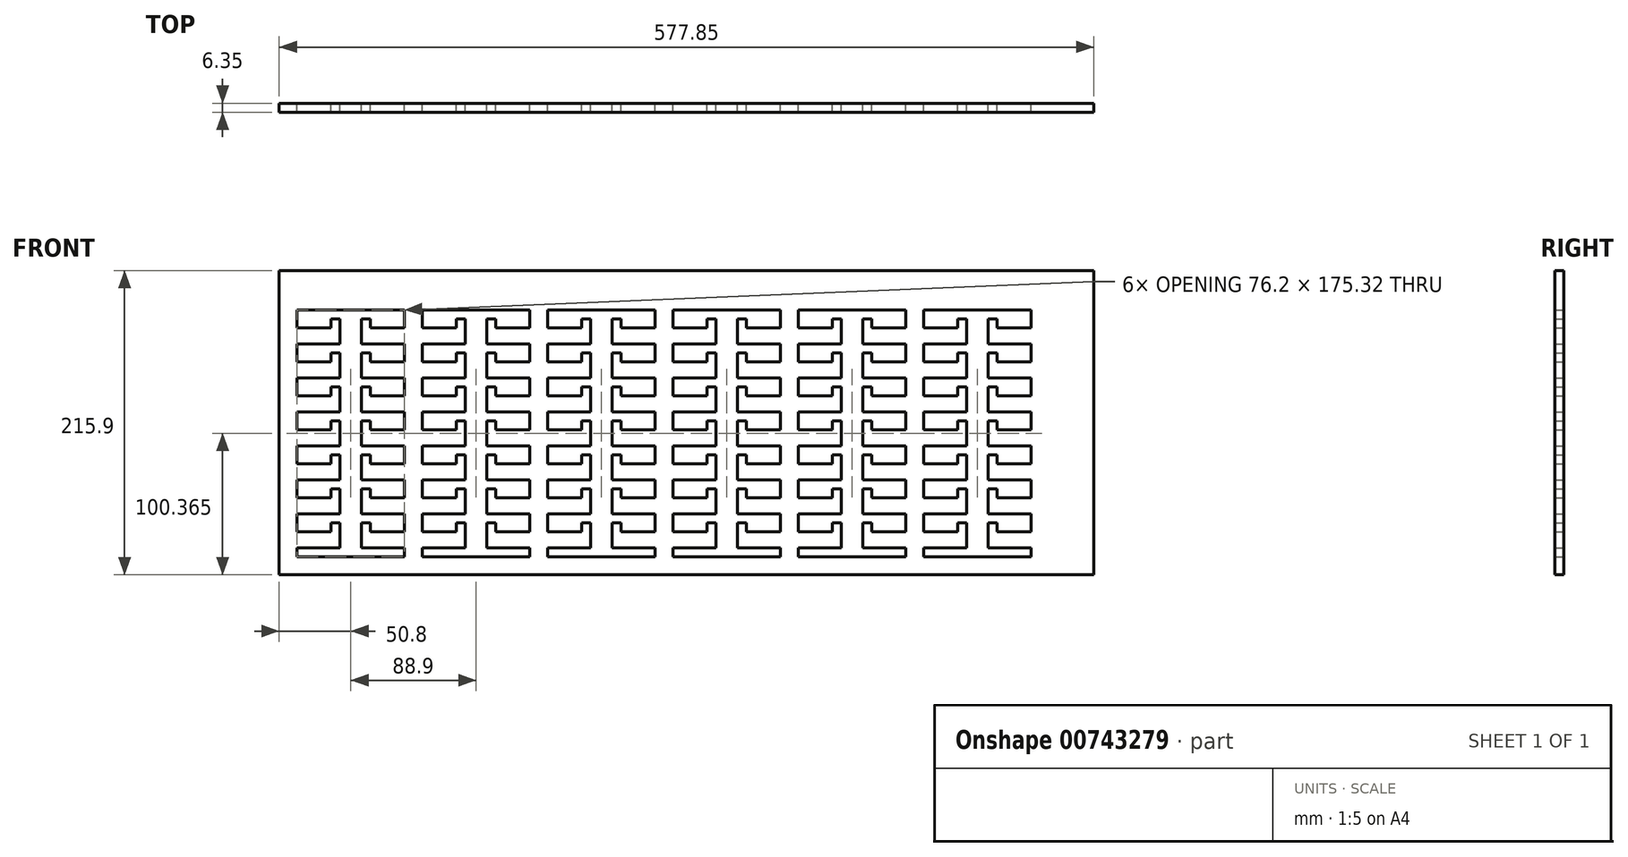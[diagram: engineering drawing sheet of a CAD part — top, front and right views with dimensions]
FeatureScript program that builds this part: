
annotation { "Feature Type Name" : "Feature", "Feature Type Description" : "" }
export const myFeature = defineFeature(function(context is Context, id is Id, definition is map)
    precondition{}
    {
        {
            var Q0;
            Q0=qCreatedBy(makeId("Front.planeOp"),FACE);
            var sketch = newSketch(context, id + "F0", { "sketchPlane" : qUnion([Q0])});
            skLineSegment(sketch, "E0", {"start": v(-97.96, -49.5) * mm, "end": v(-67.48, -49.5) * mm});
            skLineSegment(sketch, "E1", {"start": v(-67.48, -49.5) * mm, "end": v(-67.48, -31.72) * mm});
            skLineSegment(sketch, "E2", {"start": v(-67.48, -31.72) * mm, "end": v(-73.83, -31.72) * mm});
            skLineSegment(sketch, "E3", {"start": v(-73.83, -31.72) * mm, "end": v(-73.83, -38.07) * mm});
            skLineSegment(sketch, "E4", {"start": v(-73.83, -38.07) * mm, "end": v(-97.96, -38.07) * mm});
            skLineSegment(sketch, "E5", {"start": v(-97.96, -38.07) * mm, "end": v(-97.96, -25.37) * mm});
            skLineSegment(sketch, "E6", {"start": v(-97.96, -25.37) * mm, "end": v(-67.48, -25.37) * mm});
            skLineSegment(sketch, "E7", {"start": v(-67.48, -25.37) * mm, "end": v(-67.48, -7.6) * mm});
            skLineSegment(sketch, "E8", {"start": v(-67.48, -7.6) * mm, "end": v(-73.83, -7.6) * mm});
            skLineSegment(sketch, "E9", {"start": v(-73.83, -7.6) * mm, "end": v(-73.83, -13.94) * mm});
            skLineSegment(sketch, "E10", {"start": v(-73.83, -13.94) * mm, "end": v(-97.96, -13.94) * mm});
            skLineSegment(sketch, "E11", {"start": v(-97.96, -13.94) * mm, "end": v(-97.96, -1.24) * mm});
            skLineSegment(sketch, "E12", {"start": v(-97.96, -1.24) * mm, "end": v(-67.48, -1.24) * mm});
            skLineSegment(sketch, "E13", {"start": v(-67.48, -1.24) * mm, "end": v(-67.48, 16.54) * mm});
            skLineSegment(sketch, "E14", {"start": v(-67.48, 16.54) * mm, "end": v(-73.83, 16.54) * mm});
            skLineSegment(sketch, "E15", {"start": v(-73.83, 16.54) * mm, "end": v(-73.83, 10.19) * mm});
            skLineSegment(sketch, "E16", {"start": v(-73.83, 10.19) * mm, "end": v(-97.96, 10.19) * mm});
            skLineSegment(sketch, "E17", {"start": v(-97.96, 10.19) * mm, "end": v(-97.96, 22.89) * mm});
            skLineSegment(sketch, "E18", {"start": v(-97.96, 22.89) * mm, "end": v(-67.48, 22.89) * mm});
            skLineSegment(sketch, "E19", {"start": v(-67.48, 22.89) * mm, "end": v(-67.48, 40.67) * mm});
            skLineSegment(sketch, "E20", {"start": v(-67.48, 40.67) * mm, "end": v(-73.83, 40.67) * mm});
            skLineSegment(sketch, "E21", {"start": v(-73.83, 40.67) * mm, "end": v(-73.83, 34.32) * mm});
            skLineSegment(sketch, "E22", {"start": v(-73.83, 34.32) * mm, "end": v(-97.96, 34.32) * mm});
            skLineSegment(sketch, "E23", {"start": v(-97.96, 34.32) * mm, "end": v(-97.96, 47.02) * mm});
            skLineSegment(sketch, "E24", {"start": v(-21.76, -80.05) * mm, "end": v(-21.76, -73.63) * mm});
            skLineSegment(sketch, "E25", {"start": v(-21.76, -73.63) * mm, "end": v(-52.24, -73.63) * mm});
            skLineSegment(sketch, "E26", {"start": v(-52.24, -73.63) * mm, "end": v(-52.24, -55.85) * mm});
            skLineSegment(sketch, "E27", {"start": v(-52.24, -55.85) * mm, "end": v(-45.89, -55.85) * mm});
            skLineSegment(sketch, "E28", {"start": v(-45.89, -55.85) * mm, "end": v(-45.89, -62.2) * mm});
            skLineSegment(sketch, "E29", {"start": v(-45.89, -62.2) * mm, "end": v(-21.76, -62.2) * mm});
            skLineSegment(sketch, "E30", {"start": v(-21.76, -62.2) * mm, "end": v(-21.76, -49.5) * mm});
            skLineSegment(sketch, "E31", {"start": v(-21.76, -49.5) * mm, "end": v(-52.24, -49.5) * mm});
            skLineSegment(sketch, "E32", {"start": v(-52.24, -49.5) * mm, "end": v(-52.24, -31.72) * mm});
            skLineSegment(sketch, "E33", {"start": v(-52.24, -31.72) * mm, "end": v(-45.89, -31.72) * mm});
            skLineSegment(sketch, "E34", {"start": v(-45.89, -31.72) * mm, "end": v(-45.89, -38.07) * mm});
            skLineSegment(sketch, "E35", {"start": v(-45.89, -38.07) * mm, "end": v(-21.76, -38.07) * mm});
            skLineSegment(sketch, "E36", {"start": v(-21.76, -38.07) * mm, "end": v(-21.76, -25.37) * mm});
            skLineSegment(sketch, "E37", {"start": v(-21.76, -25.37) * mm, "end": v(-52.24, -25.37) * mm});
            skLineSegment(sketch, "E38", {"start": v(-52.24, -25.37) * mm, "end": v(-52.24, -7.6) * mm});
            skLineSegment(sketch, "E39", {"start": v(-52.24, -7.6) * mm, "end": v(-45.89, -7.6) * mm});
            skLineSegment(sketch, "E40", {"start": v(-45.89, -7.6) * mm, "end": v(-45.89, -13.94) * mm});
            skLineSegment(sketch, "E41", {"start": v(-45.89, -13.94) * mm, "end": v(-21.76, -13.94) * mm});
            skLineSegment(sketch, "E42", {"start": v(-21.76, -13.94) * mm, "end": v(-21.76, -1.24) * mm});
            skLineSegment(sketch, "E43", {"start": v(-21.76, -1.24) * mm, "end": v(-52.24, -1.24) * mm});
            skLineSegment(sketch, "E44", {"start": v(-52.24, -1.24) * mm, "end": v(-52.24, 16.54) * mm});
            skLineSegment(sketch, "E45", {"start": v(-52.24, 16.54) * mm, "end": v(-45.89, 16.54) * mm});
            skLineSegment(sketch, "E46", {"start": v(-45.89, 16.54) * mm, "end": v(-45.89, 10.19) * mm});
            skLineSegment(sketch, "E47", {"start": v(-45.89, 10.19) * mm, "end": v(-21.76, 10.19) * mm});
            skLineSegment(sketch, "E48", {"start": v(-21.76, 10.19) * mm, "end": v(-21.76, 22.89) * mm});
            skLineSegment(sketch, "E49", {"start": v(-21.76, 22.89) * mm, "end": v(-52.24, 22.89) * mm});
            skLineSegment(sketch, "E50", {"start": v(-52.24, 22.89) * mm, "end": v(-52.24, 40.67) * mm});
            skLineSegment(sketch, "E51", {"start": v(-52.24, 40.67) * mm, "end": v(-45.89, 40.67) * mm});
            skLineSegment(sketch, "E52", {"start": v(-45.89, 40.67) * mm, "end": v(-45.89, 34.32) * mm});
            skLineSegment(sketch, "E53", {"start": v(-45.89, 34.32) * mm, "end": v(-21.76, 34.32) * mm});
            skLineSegment(sketch, "E54", {"start": v(-21.76, 34.32) * mm, "end": v(-21.76, 47.02) * mm});
            skLineSegment(sketch, "E55", {"start": v(-67.48, -73.63) * mm, "end": v(-67.48, -55.85) * mm});
            skLineSegment(sketch, "E56", {"start": v(-73.83, -62.2) * mm, "end": v(-73.83, -55.85) * mm});
            skLineSegment(sketch, "E57", {"start": v(-73.83, -55.85) * mm, "end": v(-67.48, -55.85) * mm});
            skLineSegment(sketch, "E58", {"start": v(-67.48, -73.63) * mm, "end": v(-97.96, -73.63) * mm});
            skLineSegment(sketch, "E59", {"start": v(-97.96, -62.2) * mm, "end": v(-97.96, -49.5) * mm});
            skLineSegment(sketch, "E60", {"start": v(-97.96, -73.63) * mm, "end": v(-97.96, -80.05) * mm});
            skLineSegment(sketch, "E61", {"start": v(-97.96, -62.2) * mm, "end": v(-73.83, -62.2) * mm});
            skLineSegment(sketch, "E62", {"start": v(-97.96, -80.05) * mm, "end": v(-21.76, -80.05) * mm});
            skPoint(sketch, "E63", {"position": v(-59.86, -80.05) * mm});
            skLineSegment(sketch, "E64", {"start": v(-186.86, -49.5) * mm, "end": v(-156.38, -49.5) * mm});
            skLineSegment(sketch, "E65", {"start": v(-156.38, -49.5) * mm, "end": v(-156.38, -31.72) * mm});
            skLineSegment(sketch, "E66", {"start": v(-156.38, -31.72) * mm, "end": v(-162.73, -31.72) * mm});
            skLineSegment(sketch, "E67", {"start": v(-162.73, -31.72) * mm, "end": v(-162.73, -38.07) * mm});
            skLineSegment(sketch, "E68", {"start": v(-162.73, -38.07) * mm, "end": v(-186.86, -38.07) * mm});
            skLineSegment(sketch, "E69", {"start": v(-186.86, -38.07) * mm, "end": v(-186.86, -25.37) * mm});
            skLineSegment(sketch, "E70", {"start": v(-186.86, -25.37) * mm, "end": v(-156.38, -25.37) * mm});
            skLineSegment(sketch, "E71", {"start": v(-156.38, -25.37) * mm, "end": v(-156.38, -7.6) * mm});
            skLineSegment(sketch, "E72", {"start": v(-156.38, -7.6) * mm, "end": v(-162.73, -7.6) * mm});
            skLineSegment(sketch, "E73", {"start": v(-162.73, -7.6) * mm, "end": v(-162.73, -13.94) * mm});
            skLineSegment(sketch, "E74", {"start": v(-162.73, -13.94) * mm, "end": v(-186.86, -13.94) * mm});
            skLineSegment(sketch, "E75", {"start": v(-186.86, -13.94) * mm, "end": v(-186.86, -1.24) * mm});
            skLineSegment(sketch, "E76", {"start": v(-186.86, -1.24) * mm, "end": v(-156.38, -1.24) * mm});
            skLineSegment(sketch, "E77", {"start": v(-156.38, -1.24) * mm, "end": v(-156.38, 16.54) * mm});
            skLineSegment(sketch, "E78", {"start": v(-156.38, 16.54) * mm, "end": v(-162.73, 16.54) * mm});
            skLineSegment(sketch, "E79", {"start": v(-162.73, 16.54) * mm, "end": v(-162.73, 10.19) * mm});
            skLineSegment(sketch, "E80", {"start": v(-162.73, 10.19) * mm, "end": v(-186.86, 10.19) * mm});
            skLineSegment(sketch, "E81", {"start": v(-186.86, 10.19) * mm, "end": v(-186.86, 22.89) * mm});
            skLineSegment(sketch, "E82", {"start": v(-186.86, 22.89) * mm, "end": v(-156.38, 22.89) * mm});
            skLineSegment(sketch, "E83", {"start": v(-156.38, 22.89) * mm, "end": v(-156.38, 40.67) * mm});
            skLineSegment(sketch, "E84", {"start": v(-156.38, 40.67) * mm, "end": v(-162.73, 40.67) * mm});
            skLineSegment(sketch, "E85", {"start": v(-162.73, 40.67) * mm, "end": v(-162.73, 34.32) * mm});
            skLineSegment(sketch, "E86", {"start": v(-162.73, 34.32) * mm, "end": v(-186.86, 34.32) * mm});
            skLineSegment(sketch, "E87", {"start": v(-186.86, 34.32) * mm, "end": v(-186.86, 47.02) * mm});
            skLineSegment(sketch, "E88", {"start": v(-110.66, -80.05) * mm, "end": v(-110.66, -73.63) * mm});
            skLineSegment(sketch, "E89", {"start": v(-110.66, -73.63) * mm, "end": v(-141.14, -73.63) * mm});
            skLineSegment(sketch, "E90", {"start": v(-141.14, -73.63) * mm, "end": v(-141.14, -55.85) * mm});
            skLineSegment(sketch, "E91", {"start": v(-141.14, -55.85) * mm, "end": v(-134.79, -55.85) * mm});
            skLineSegment(sketch, "E92", {"start": v(-134.79, -55.85) * mm, "end": v(-134.79, -62.2) * mm});
            skLineSegment(sketch, "E93", {"start": v(-134.79, -62.2) * mm, "end": v(-110.66, -62.2) * mm});
            skLineSegment(sketch, "E94", {"start": v(-110.66, -62.2) * mm, "end": v(-110.66, -49.5) * mm});
            skLineSegment(sketch, "E95", {"start": v(-110.66, -49.5) * mm, "end": v(-141.14, -49.5) * mm});
            skLineSegment(sketch, "E96", {"start": v(-141.14, -49.5) * mm, "end": v(-141.14, -31.72) * mm});
            skLineSegment(sketch, "E97", {"start": v(-141.14, -31.72) * mm, "end": v(-134.79, -31.72) * mm});
            skLineSegment(sketch, "E98", {"start": v(-134.79, -31.72) * mm, "end": v(-134.79, -38.07) * mm});
            skLineSegment(sketch, "E99", {"start": v(-134.79, -38.07) * mm, "end": v(-110.66, -38.07) * mm});
            skLineSegment(sketch, "E100", {"start": v(-110.66, -38.07) * mm, "end": v(-110.66, -25.37) * mm});
            skLineSegment(sketch, "E101", {"start": v(-110.66, -25.37) * mm, "end": v(-141.14, -25.37) * mm});
            skLineSegment(sketch, "E102", {"start": v(-141.14, -25.37) * mm, "end": v(-141.14, -7.6) * mm});
            skLineSegment(sketch, "E103", {"start": v(-141.14, -7.6) * mm, "end": v(-134.79, -7.6) * mm});
            skLineSegment(sketch, "E104", {"start": v(-134.79, -7.6) * mm, "end": v(-134.79, -13.94) * mm});
            skLineSegment(sketch, "E105", {"start": v(-134.79, -13.94) * mm, "end": v(-110.66, -13.94) * mm});
            skLineSegment(sketch, "E106", {"start": v(-110.66, -13.94) * mm, "end": v(-110.66, -1.24) * mm});
            skLineSegment(sketch, "E107", {"start": v(-110.66, -1.24) * mm, "end": v(-141.14, -1.24) * mm});
            skLineSegment(sketch, "E108", {"start": v(-141.14, -1.24) * mm, "end": v(-141.14, 16.54) * mm});
            skLineSegment(sketch, "E109", {"start": v(-141.14, 16.54) * mm, "end": v(-134.79, 16.54) * mm});
            skLineSegment(sketch, "E110", {"start": v(-134.79, 16.54) * mm, "end": v(-134.79, 10.19) * mm});
            skLineSegment(sketch, "E111", {"start": v(-134.79, 10.19) * mm, "end": v(-110.66, 10.19) * mm});
            skLineSegment(sketch, "E112", {"start": v(-110.66, 10.19) * mm, "end": v(-110.66, 22.89) * mm});
            skLineSegment(sketch, "E113", {"start": v(-110.66, 22.89) * mm, "end": v(-141.14, 22.89) * mm});
            skLineSegment(sketch, "E114", {"start": v(-141.14, 22.89) * mm, "end": v(-141.14, 40.67) * mm});
            skLineSegment(sketch, "E115", {"start": v(-141.14, 40.67) * mm, "end": v(-134.79, 40.67) * mm});
            skLineSegment(sketch, "E116", {"start": v(-134.79, 40.67) * mm, "end": v(-134.79, 34.32) * mm});
            skLineSegment(sketch, "E117", {"start": v(-134.79, 34.32) * mm, "end": v(-110.66, 34.32) * mm});
            skLineSegment(sketch, "E118", {"start": v(-110.66, 34.32) * mm, "end": v(-110.66, 47.02) * mm});
            skLineSegment(sketch, "E119", {"start": v(-156.38, -73.63) * mm, "end": v(-156.38, -55.85) * mm});
            skLineSegment(sketch, "E120", {"start": v(-162.73, -62.2) * mm, "end": v(-162.73, -55.85) * mm});
            skLineSegment(sketch, "E121", {"start": v(-162.73, -55.85) * mm, "end": v(-156.38, -55.85) * mm});
            skLineSegment(sketch, "E122", {"start": v(-156.38, -73.63) * mm, "end": v(-186.86, -73.63) * mm});
            skLineSegment(sketch, "E123", {"start": v(-186.86, -62.2) * mm, "end": v(-186.86, -49.5) * mm});
            skLineSegment(sketch, "E124", {"start": v(-186.86, -73.63) * mm, "end": v(-186.86, -80.05) * mm});
            skLineSegment(sketch, "E125", {"start": v(-186.86, -62.2) * mm, "end": v(-162.73, -62.2) * mm});
            skLineSegment(sketch, "E126", {"start": v(-186.86, -80.05) * mm, "end": v(-110.66, -80.05) * mm});
            skPoint(sketch, "E127", {"position": v(-148.76, -80.05) * mm});
            skLineSegment(sketch, "E128", {"start": v(-275.76, -49.5) * mm, "end": v(-245.28, -49.5) * mm});
            skLineSegment(sketch, "E129", {"start": v(-245.28, -49.5) * mm, "end": v(-245.28, -31.72) * mm});
            skLineSegment(sketch, "E130", {"start": v(-245.28, -31.72) * mm, "end": v(-251.63, -31.72) * mm});
            skLineSegment(sketch, "E131", {"start": v(-251.63, -31.72) * mm, "end": v(-251.63, -38.07) * mm});
            skLineSegment(sketch, "E132", {"start": v(-251.63, -38.07) * mm, "end": v(-275.76, -38.07) * mm});
            skLineSegment(sketch, "E133", {"start": v(-275.76, -38.07) * mm, "end": v(-275.76, -25.37) * mm});
            skLineSegment(sketch, "E134", {"start": v(-275.76, -25.37) * mm, "end": v(-245.28, -25.37) * mm});
            skLineSegment(sketch, "E135", {"start": v(-245.28, -25.37) * mm, "end": v(-245.28, -7.6) * mm});
            skLineSegment(sketch, "E136", {"start": v(-245.28, -7.6) * mm, "end": v(-251.63, -7.6) * mm});
            skLineSegment(sketch, "E137", {"start": v(-251.63, -7.6) * mm, "end": v(-251.63, -13.94) * mm});
            skLineSegment(sketch, "E138", {"start": v(-251.63, -13.94) * mm, "end": v(-275.76, -13.94) * mm});
            skLineSegment(sketch, "E139", {"start": v(-275.76, -13.94) * mm, "end": v(-275.76, -1.24) * mm});
            skLineSegment(sketch, "E140", {"start": v(-275.76, -1.24) * mm, "end": v(-245.28, -1.24) * mm});
            skLineSegment(sketch, "E141", {"start": v(-245.28, -1.24) * mm, "end": v(-245.28, 16.54) * mm});
            skLineSegment(sketch, "E142", {"start": v(-245.28, 16.54) * mm, "end": v(-251.63, 16.54) * mm});
            skLineSegment(sketch, "E143", {"start": v(-251.63, 16.54) * mm, "end": v(-251.63, 10.19) * mm});
            skLineSegment(sketch, "E144", {"start": v(-251.63, 10.19) * mm, "end": v(-275.76, 10.19) * mm});
            skLineSegment(sketch, "E145", {"start": v(-275.76, 10.19) * mm, "end": v(-275.76, 22.89) * mm});
            skLineSegment(sketch, "E146", {"start": v(-275.76, 22.89) * mm, "end": v(-245.28, 22.89) * mm});
            skLineSegment(sketch, "E147", {"start": v(-245.28, 22.89) * mm, "end": v(-245.28, 40.67) * mm});
            skLineSegment(sketch, "E148", {"start": v(-245.28, 40.67) * mm, "end": v(-251.63, 40.67) * mm});
            skLineSegment(sketch, "E149", {"start": v(-251.63, 40.67) * mm, "end": v(-251.63, 34.32) * mm});
            skLineSegment(sketch, "E150", {"start": v(-251.63, 34.32) * mm, "end": v(-275.76, 34.32) * mm});
            skLineSegment(sketch, "E151", {"start": v(-275.76, 34.32) * mm, "end": v(-275.76, 47.02) * mm});
            skLineSegment(sketch, "E152", {"start": v(-199.56, -80.05) * mm, "end": v(-199.56, -73.63) * mm});
            skLineSegment(sketch, "E153", {"start": v(-199.56, -73.63) * mm, "end": v(-230.04, -73.63) * mm});
            skLineSegment(sketch, "E154", {"start": v(-230.04, -73.63) * mm, "end": v(-230.04, -55.85) * mm});
            skLineSegment(sketch, "E155", {"start": v(-230.04, -55.85) * mm, "end": v(-223.69, -55.85) * mm});
            skLineSegment(sketch, "E156", {"start": v(-223.69, -55.85) * mm, "end": v(-223.69, -62.2) * mm});
            skLineSegment(sketch, "E157", {"start": v(-223.69, -62.2) * mm, "end": v(-199.56, -62.2) * mm});
            skLineSegment(sketch, "E158", {"start": v(-199.56, -62.2) * mm, "end": v(-199.56, -49.5) * mm});
            skLineSegment(sketch, "E159", {"start": v(-199.56, -49.5) * mm, "end": v(-230.04, -49.5) * mm});
            skLineSegment(sketch, "E160", {"start": v(-230.04, -49.5) * mm, "end": v(-230.04, -31.72) * mm});
            skLineSegment(sketch, "E161", {"start": v(-230.04, -31.72) * mm, "end": v(-223.69, -31.72) * mm});
            skLineSegment(sketch, "E162", {"start": v(-223.69, -31.72) * mm, "end": v(-223.69, -38.07) * mm});
            skLineSegment(sketch, "E163", {"start": v(-223.69, -38.07) * mm, "end": v(-199.56, -38.07) * mm});
            skLineSegment(sketch, "E164", {"start": v(-199.56, -38.07) * mm, "end": v(-199.56, -25.37) * mm});
            skLineSegment(sketch, "E165", {"start": v(-199.56, -25.37) * mm, "end": v(-230.04, -25.37) * mm});
            skLineSegment(sketch, "E166", {"start": v(-230.04, -25.37) * mm, "end": v(-230.04, -7.6) * mm});
            skLineSegment(sketch, "E167", {"start": v(-230.04, -7.6) * mm, "end": v(-223.69, -7.6) * mm});
            skLineSegment(sketch, "E168", {"start": v(-223.69, -7.6) * mm, "end": v(-223.69, -13.94) * mm});
            skLineSegment(sketch, "E169", {"start": v(-223.69, -13.94) * mm, "end": v(-199.56, -13.94) * mm});
            skLineSegment(sketch, "E170", {"start": v(-199.56, -13.94) * mm, "end": v(-199.56, -1.24) * mm});
            skLineSegment(sketch, "E171", {"start": v(-199.56, -1.24) * mm, "end": v(-230.04, -1.24) * mm});
            skLineSegment(sketch, "E172", {"start": v(-230.04, -1.24) * mm, "end": v(-230.04, 16.54) * mm});
            skLineSegment(sketch, "E173", {"start": v(-230.04, 16.54) * mm, "end": v(-223.69, 16.54) * mm});
            skLineSegment(sketch, "E174", {"start": v(-223.69, 16.54) * mm, "end": v(-223.69, 10.19) * mm});
            skLineSegment(sketch, "E175", {"start": v(-223.69, 10.19) * mm, "end": v(-199.56, 10.19) * mm});
            skLineSegment(sketch, "E176", {"start": v(-199.56, 10.19) * mm, "end": v(-199.56, 22.89) * mm});
            skLineSegment(sketch, "E177", {"start": v(-199.56, 22.89) * mm, "end": v(-230.04, 22.89) * mm});
            skLineSegment(sketch, "E178", {"start": v(-230.04, 22.89) * mm, "end": v(-230.04, 40.67) * mm});
            skLineSegment(sketch, "E179", {"start": v(-230.04, 40.67) * mm, "end": v(-223.69, 40.67) * mm});
            skLineSegment(sketch, "E180", {"start": v(-223.69, 40.67) * mm, "end": v(-223.69, 34.32) * mm});
            skLineSegment(sketch, "E181", {"start": v(-223.69, 34.32) * mm, "end": v(-199.56, 34.32) * mm});
            skLineSegment(sketch, "E182", {"start": v(-199.56, 34.32) * mm, "end": v(-199.56, 47.02) * mm});
            skLineSegment(sketch, "E183", {"start": v(-245.28, -73.63) * mm, "end": v(-245.28, -55.85) * mm});
            skLineSegment(sketch, "E184", {"start": v(-251.63, -62.2) * mm, "end": v(-251.63, -55.85) * mm});
            skLineSegment(sketch, "E185", {"start": v(-251.63, -55.85) * mm, "end": v(-245.28, -55.85) * mm});
            skLineSegment(sketch, "E186", {"start": v(-245.28, -73.63) * mm, "end": v(-275.76, -73.63) * mm});
            skLineSegment(sketch, "E187", {"start": v(-275.76, -62.2) * mm, "end": v(-275.76, -49.5) * mm});
            skLineSegment(sketch, "E188", {"start": v(-275.76, -73.63) * mm, "end": v(-275.76, -80.05) * mm});
            skLineSegment(sketch, "E189", {"start": v(-275.76, -62.2) * mm, "end": v(-251.63, -62.2) * mm});
            skLineSegment(sketch, "E190", {"start": v(-275.76, -80.05) * mm, "end": v(-199.56, -80.05) * mm});
            skPoint(sketch, "E191", {"position": v(-237.66, -80.05) * mm});
            skLineSegment(sketch, "E192", {"start": v(-364.66, -49.5) * mm, "end": v(-334.18, -49.5) * mm});
            skLineSegment(sketch, "E193", {"start": v(-334.18, -49.5) * mm, "end": v(-334.18, -31.72) * mm});
            skLineSegment(sketch, "E194", {"start": v(-334.18, -31.72) * mm, "end": v(-340.53, -31.72) * mm});
            skLineSegment(sketch, "E195", {"start": v(-340.53, -31.72) * mm, "end": v(-340.53, -38.07) * mm});
            skLineSegment(sketch, "E196", {"start": v(-340.53, -38.07) * mm, "end": v(-364.66, -38.07) * mm});
            skLineSegment(sketch, "E197", {"start": v(-364.66, -38.07) * mm, "end": v(-364.66, -25.37) * mm});
            skLineSegment(sketch, "E198", {"start": v(-364.66, -25.37) * mm, "end": v(-334.18, -25.37) * mm});
            skLineSegment(sketch, "E199", {"start": v(-334.18, -25.37) * mm, "end": v(-334.18, -7.6) * mm});
            skLineSegment(sketch, "E200", {"start": v(-334.18, -7.6) * mm, "end": v(-340.53, -7.6) * mm});
            skLineSegment(sketch, "E201", {"start": v(-340.53, -7.6) * mm, "end": v(-340.53, -13.94) * mm});
            skLineSegment(sketch, "E202", {"start": v(-340.53, -13.94) * mm, "end": v(-364.66, -13.94) * mm});
            skLineSegment(sketch, "E203", {"start": v(-364.66, -13.94) * mm, "end": v(-364.66, -1.24) * mm});
            skLineSegment(sketch, "E204", {"start": v(-364.66, -1.24) * mm, "end": v(-334.18, -1.24) * mm});
            skLineSegment(sketch, "E205", {"start": v(-334.18, -1.24) * mm, "end": v(-334.18, 16.54) * mm});
            skLineSegment(sketch, "E206", {"start": v(-334.18, 16.54) * mm, "end": v(-340.53, 16.54) * mm});
            skLineSegment(sketch, "E207", {"start": v(-340.53, 16.54) * mm, "end": v(-340.53, 10.19) * mm});
            skLineSegment(sketch, "E208", {"start": v(-340.53, 10.19) * mm, "end": v(-364.66, 10.19) * mm});
            skLineSegment(sketch, "E209", {"start": v(-364.66, 10.19) * mm, "end": v(-364.66, 22.89) * mm});
            skLineSegment(sketch, "E210", {"start": v(-364.66, 22.89) * mm, "end": v(-334.18, 22.89) * mm});
            skLineSegment(sketch, "E211", {"start": v(-334.18, 22.89) * mm, "end": v(-334.18, 40.67) * mm});
            skLineSegment(sketch, "E212", {"start": v(-334.18, 40.67) * mm, "end": v(-340.53, 40.67) * mm});
            skLineSegment(sketch, "E213", {"start": v(-340.53, 40.67) * mm, "end": v(-340.53, 34.32) * mm});
            skLineSegment(sketch, "E214", {"start": v(-340.53, 34.32) * mm, "end": v(-364.66, 34.32) * mm});
            skLineSegment(sketch, "E215", {"start": v(-364.66, 34.32) * mm, "end": v(-364.66, 47.02) * mm});
            skLineSegment(sketch, "E216", {"start": v(-288.46, -80.05) * mm, "end": v(-288.46, -73.63) * mm});
            skLineSegment(sketch, "E217", {"start": v(-288.46, -73.63) * mm, "end": v(-318.94, -73.63) * mm});
            skLineSegment(sketch, "E218", {"start": v(-318.94, -73.63) * mm, "end": v(-318.94, -55.85) * mm});
            skLineSegment(sketch, "E219", {"start": v(-318.94, -55.85) * mm, "end": v(-312.59, -55.85) * mm});
            skLineSegment(sketch, "E220", {"start": v(-312.59, -55.85) * mm, "end": v(-312.59, -62.2) * mm});
            skLineSegment(sketch, "E221", {"start": v(-312.59, -62.2) * mm, "end": v(-288.46, -62.2) * mm});
            skLineSegment(sketch, "E222", {"start": v(-288.46, -62.2) * mm, "end": v(-288.46, -49.5) * mm});
            skLineSegment(sketch, "E223", {"start": v(-288.46, -49.5) * mm, "end": v(-318.94, -49.5) * mm});
            skLineSegment(sketch, "E224", {"start": v(-318.94, -49.5) * mm, "end": v(-318.94, -31.72) * mm});
            skLineSegment(sketch, "E225", {"start": v(-318.94, -31.72) * mm, "end": v(-312.59, -31.72) * mm});
            skLineSegment(sketch, "E226", {"start": v(-312.59, -31.72) * mm, "end": v(-312.59, -38.07) * mm});
            skLineSegment(sketch, "E227", {"start": v(-312.59, -38.07) * mm, "end": v(-288.46, -38.07) * mm});
            skLineSegment(sketch, "E228", {"start": v(-288.46, -38.07) * mm, "end": v(-288.46, -25.37) * mm});
            skLineSegment(sketch, "E229", {"start": v(-288.46, -25.37) * mm, "end": v(-318.94, -25.37) * mm});
            skLineSegment(sketch, "E230", {"start": v(-318.94, -25.37) * mm, "end": v(-318.94, -7.6) * mm});
            skLineSegment(sketch, "E231", {"start": v(-318.94, -7.6) * mm, "end": v(-312.59, -7.6) * mm});
            skLineSegment(sketch, "E232", {"start": v(-312.59, -7.6) * mm, "end": v(-312.59, -13.94) * mm});
            skLineSegment(sketch, "E233", {"start": v(-312.59, -13.94) * mm, "end": v(-288.46, -13.94) * mm});
            skLineSegment(sketch, "E234", {"start": v(-288.46, -13.94) * mm, "end": v(-288.46, -1.24) * mm});
            skLineSegment(sketch, "E235", {"start": v(-288.46, -1.24) * mm, "end": v(-318.94, -1.24) * mm});
            skLineSegment(sketch, "E236", {"start": v(-318.94, -1.24) * mm, "end": v(-318.94, 16.54) * mm});
            skLineSegment(sketch, "E237", {"start": v(-318.94, 16.54) * mm, "end": v(-312.59, 16.54) * mm});
            skLineSegment(sketch, "E238", {"start": v(-312.59, 16.54) * mm, "end": v(-312.59, 10.19) * mm});
            skLineSegment(sketch, "E239", {"start": v(-312.59, 10.19) * mm, "end": v(-288.46, 10.19) * mm});
            skLineSegment(sketch, "E240", {"start": v(-288.46, 10.19) * mm, "end": v(-288.46, 22.89) * mm});
            skLineSegment(sketch, "E241", {"start": v(-288.46, 22.89) * mm, "end": v(-318.94, 22.89) * mm});
            skLineSegment(sketch, "E242", {"start": v(-318.94, 22.89) * mm, "end": v(-318.94, 40.67) * mm});
            skLineSegment(sketch, "E243", {"start": v(-318.94, 40.67) * mm, "end": v(-312.59, 40.67) * mm});
            skLineSegment(sketch, "E244", {"start": v(-312.59, 40.67) * mm, "end": v(-312.59, 34.32) * mm});
            skLineSegment(sketch, "E245", {"start": v(-312.59, 34.32) * mm, "end": v(-288.46, 34.32) * mm});
            skLineSegment(sketch, "E246", {"start": v(-288.46, 34.32) * mm, "end": v(-288.46, 47.02) * mm});
            skLineSegment(sketch, "E247", {"start": v(-334.18, -73.63) * mm, "end": v(-334.18, -55.85) * mm});
            skLineSegment(sketch, "E248", {"start": v(-340.53, -62.2) * mm, "end": v(-340.53, -55.85) * mm});
            skLineSegment(sketch, "E249", {"start": v(-340.53, -55.85) * mm, "end": v(-334.18, -55.85) * mm});
            skLineSegment(sketch, "E250", {"start": v(-334.18, -73.63) * mm, "end": v(-364.66, -73.63) * mm});
            skLineSegment(sketch, "E251", {"start": v(-364.66, -62.2) * mm, "end": v(-364.66, -49.5) * mm});
            skLineSegment(sketch, "E252", {"start": v(-364.66, -73.63) * mm, "end": v(-364.66, -80.05) * mm});
            skLineSegment(sketch, "E253", {"start": v(-364.66, -62.2) * mm, "end": v(-340.53, -62.2) * mm});
            skLineSegment(sketch, "E254", {"start": v(-364.66, -80.05) * mm, "end": v(-288.46, -80.05) * mm});
            skPoint(sketch, "E255", {"position": v(-326.56, -80.05) * mm});
            skLineSegment(sketch, "E256.bottom", {"start": v(22.7, 123.15) * mm, "end": v(-555.16, 123.15) * mm});
            skLineSegment(sketch, "E256.top", {"start": v(22.7, -92.75) * mm, "end": v(-555.16, -92.75) * mm});
            skLineSegment(sketch, "E256.left", {"start": v(22.7, 123.15) * mm, "end": v(22.7, -92.75) * mm});
            skLineSegment(sketch, "E256.right", {"start": v(-555.16, 123.15) * mm, "end": v(-555.16, -92.75) * mm});
            skPoint(sketch, "E257", {"position": v(-266.23, 123.15) * mm});
            skLineSegment(sketch, "E258", {"start": v(-453.56, -49.5) * mm, "end": v(-423.08, -49.5) * mm});
            skLineSegment(sketch, "E259", {"start": v(-423.08, -49.5) * mm, "end": v(-423.08, -31.72) * mm});
            skLineSegment(sketch, "E260", {"start": v(-423.08, -31.72) * mm, "end": v(-429.43, -31.72) * mm});
            skLineSegment(sketch, "E261", {"start": v(-429.43, -31.72) * mm, "end": v(-429.43, -38.07) * mm});
            skLineSegment(sketch, "E262", {"start": v(-429.43, -38.07) * mm, "end": v(-453.56, -38.07) * mm});
            skLineSegment(sketch, "E263", {"start": v(-453.56, -38.07) * mm, "end": v(-453.56, -25.37) * mm});
            skLineSegment(sketch, "E264", {"start": v(-453.56, -25.37) * mm, "end": v(-423.08, -25.37) * mm});
            skLineSegment(sketch, "E265", {"start": v(-423.08, -25.37) * mm, "end": v(-423.08, -7.6) * mm});
            skLineSegment(sketch, "E266", {"start": v(-423.08, -7.6) * mm, "end": v(-429.43, -7.6) * mm});
            skLineSegment(sketch, "E267", {"start": v(-429.43, -7.6) * mm, "end": v(-429.43, -13.94) * mm});
            skLineSegment(sketch, "E268", {"start": v(-429.43, -13.94) * mm, "end": v(-453.56, -13.94) * mm});
            skLineSegment(sketch, "E269", {"start": v(-453.56, -13.94) * mm, "end": v(-453.56, -1.24) * mm});
            skLineSegment(sketch, "E270", {"start": v(-453.56, -1.24) * mm, "end": v(-423.08, -1.24) * mm});
            skLineSegment(sketch, "E271", {"start": v(-423.08, -1.24) * mm, "end": v(-423.08, 16.54) * mm});
            skLineSegment(sketch, "E272", {"start": v(-423.08, 16.54) * mm, "end": v(-429.43, 16.54) * mm});
            skLineSegment(sketch, "E273", {"start": v(-429.43, 16.54) * mm, "end": v(-429.43, 10.19) * mm});
            skLineSegment(sketch, "E274", {"start": v(-429.43, 10.19) * mm, "end": v(-453.56, 10.19) * mm});
            skLineSegment(sketch, "E275", {"start": v(-453.56, 10.19) * mm, "end": v(-453.56, 22.89) * mm});
            skLineSegment(sketch, "E276", {"start": v(-453.56, 22.89) * mm, "end": v(-423.08, 22.89) * mm});
            skLineSegment(sketch, "E277", {"start": v(-423.08, 22.89) * mm, "end": v(-423.08, 40.67) * mm});
            skLineSegment(sketch, "E278", {"start": v(-423.08, 40.67) * mm, "end": v(-429.43, 40.67) * mm});
            skLineSegment(sketch, "E279", {"start": v(-429.43, 40.67) * mm, "end": v(-429.43, 34.32) * mm});
            skLineSegment(sketch, "E280", {"start": v(-429.43, 34.32) * mm, "end": v(-453.56, 34.32) * mm});
            skLineSegment(sketch, "E281", {"start": v(-453.56, 34.32) * mm, "end": v(-453.56, 47.02) * mm});
            skLineSegment(sketch, "E282", {"start": v(-377.36, -80.05) * mm, "end": v(-377.36, -73.63) * mm});
            skLineSegment(sketch, "E283", {"start": v(-377.36, -73.63) * mm, "end": v(-407.84, -73.63) * mm});
            skLineSegment(sketch, "E284", {"start": v(-407.84, -73.63) * mm, "end": v(-407.84, -55.85) * mm});
            skLineSegment(sketch, "E285", {"start": v(-407.84, -55.85) * mm, "end": v(-401.49, -55.85) * mm});
            skLineSegment(sketch, "E286", {"start": v(-401.49, -55.85) * mm, "end": v(-401.49, -62.2) * mm});
            skLineSegment(sketch, "E287", {"start": v(-401.49, -62.2) * mm, "end": v(-377.36, -62.2) * mm});
            skLineSegment(sketch, "E288", {"start": v(-377.36, -62.2) * mm, "end": v(-377.36, -49.5) * mm});
            skLineSegment(sketch, "E289", {"start": v(-377.36, -49.5) * mm, "end": v(-407.84, -49.5) * mm});
            skLineSegment(sketch, "E290", {"start": v(-407.84, -49.5) * mm, "end": v(-407.84, -31.72) * mm});
            skLineSegment(sketch, "E291", {"start": v(-407.84, -31.72) * mm, "end": v(-401.49, -31.72) * mm});
            skLineSegment(sketch, "E292", {"start": v(-401.49, -31.72) * mm, "end": v(-401.49, -38.07) * mm});
            skLineSegment(sketch, "E293", {"start": v(-401.49, -38.07) * mm, "end": v(-377.36, -38.07) * mm});
            skLineSegment(sketch, "E294", {"start": v(-377.36, -38.07) * mm, "end": v(-377.36, -25.37) * mm});
            skLineSegment(sketch, "E295", {"start": v(-377.36, -25.37) * mm, "end": v(-407.84, -25.37) * mm});
            skLineSegment(sketch, "E296", {"start": v(-407.84, -25.37) * mm, "end": v(-407.84, -7.6) * mm});
            skLineSegment(sketch, "E297", {"start": v(-407.84, -7.6) * mm, "end": v(-401.49, -7.6) * mm});
            skLineSegment(sketch, "E298", {"start": v(-401.49, -7.6) * mm, "end": v(-401.49, -13.94) * mm});
            skLineSegment(sketch, "E299", {"start": v(-401.49, -13.94) * mm, "end": v(-377.36, -13.94) * mm});
            skLineSegment(sketch, "E300", {"start": v(-377.36, -13.94) * mm, "end": v(-377.36, -1.24) * mm});
            skLineSegment(sketch, "E301", {"start": v(-377.36, -1.24) * mm, "end": v(-407.84, -1.24) * mm});
            skLineSegment(sketch, "E302", {"start": v(-407.84, -1.24) * mm, "end": v(-407.84, 16.54) * mm});
            skLineSegment(sketch, "E303", {"start": v(-407.84, 16.54) * mm, "end": v(-401.49, 16.54) * mm});
            skLineSegment(sketch, "E304", {"start": v(-401.49, 16.54) * mm, "end": v(-401.49, 10.19) * mm});
            skLineSegment(sketch, "E305", {"start": v(-401.49, 10.19) * mm, "end": v(-377.36, 10.19) * mm});
            skLineSegment(sketch, "E306", {"start": v(-377.36, 10.19) * mm, "end": v(-377.36, 22.89) * mm});
            skLineSegment(sketch, "E307", {"start": v(-377.36, 22.89) * mm, "end": v(-407.84, 22.89) * mm});
            skLineSegment(sketch, "E308", {"start": v(-407.84, 22.89) * mm, "end": v(-407.84, 40.67) * mm});
            skLineSegment(sketch, "E309", {"start": v(-407.84, 40.67) * mm, "end": v(-401.49, 40.67) * mm});
            skLineSegment(sketch, "E310", {"start": v(-401.49, 40.67) * mm, "end": v(-401.49, 34.32) * mm});
            skLineSegment(sketch, "E311", {"start": v(-401.49, 34.32) * mm, "end": v(-377.36, 34.32) * mm});
            skLineSegment(sketch, "E312", {"start": v(-377.36, 34.32) * mm, "end": v(-377.36, 47.02) * mm});
            skLineSegment(sketch, "E313", {"start": v(-423.08, -73.63) * mm, "end": v(-423.08, -55.85) * mm});
            skLineSegment(sketch, "E314", {"start": v(-429.43, -62.2) * mm, "end": v(-429.43, -55.85) * mm});
            skLineSegment(sketch, "E315", {"start": v(-429.43, -55.85) * mm, "end": v(-423.08, -55.85) * mm});
            skLineSegment(sketch, "E316", {"start": v(-423.08, -73.63) * mm, "end": v(-453.56, -73.63) * mm});
            skLineSegment(sketch, "E317", {"start": v(-453.56, -62.2) * mm, "end": v(-453.56, -49.5) * mm});
            skLineSegment(sketch, "E318", {"start": v(-453.56, -73.63) * mm, "end": v(-453.56, -80.05) * mm});
            skLineSegment(sketch, "E319", {"start": v(-453.56, -62.2) * mm, "end": v(-429.43, -62.2) * mm});
            skLineSegment(sketch, "E320", {"start": v(-453.56, -80.05) * mm, "end": v(-377.36, -80.05) * mm});
            skPoint(sketch, "E321", {"position": v(-415.46, -80.05) * mm});
            skLineSegment(sketch, "E322", {"start": v(-542.46, -49.5) * mm, "end": v(-511.98, -49.5) * mm});
            skLineSegment(sketch, "E323", {"start": v(-511.98, -49.5) * mm, "end": v(-511.98, -31.72) * mm});
            skLineSegment(sketch, "E324", {"start": v(-511.98, -31.72) * mm, "end": v(-518.33, -31.72) * mm});
            skLineSegment(sketch, "E325", {"start": v(-518.33, -31.72) * mm, "end": v(-518.33, -38.07) * mm});
            skLineSegment(sketch, "E326", {"start": v(-518.33, -38.07) * mm, "end": v(-542.46, -38.07) * mm});
            skLineSegment(sketch, "E327", {"start": v(-542.46, -38.07) * mm, "end": v(-542.46, -25.37) * mm});
            skLineSegment(sketch, "E328", {"start": v(-542.46, -25.37) * mm, "end": v(-511.98, -25.37) * mm});
            skLineSegment(sketch, "E329", {"start": v(-511.98, -25.37) * mm, "end": v(-511.98, -7.6) * mm});
            skLineSegment(sketch, "E330", {"start": v(-511.98, -7.6) * mm, "end": v(-518.33, -7.6) * mm});
            skLineSegment(sketch, "E331", {"start": v(-518.33, -7.6) * mm, "end": v(-518.33, -13.94) * mm});
            skLineSegment(sketch, "E332", {"start": v(-518.33, -13.94) * mm, "end": v(-542.46, -13.94) * mm});
            skLineSegment(sketch, "E333", {"start": v(-542.46, -13.94) * mm, "end": v(-542.46, -1.24) * mm});
            skLineSegment(sketch, "E334", {"start": v(-542.46, -1.24) * mm, "end": v(-511.98, -1.24) * mm});
            skLineSegment(sketch, "E335", {"start": v(-511.98, -1.24) * mm, "end": v(-511.98, 16.54) * mm});
            skLineSegment(sketch, "E336", {"start": v(-511.98, 16.54) * mm, "end": v(-518.33, 16.54) * mm});
            skLineSegment(sketch, "E337", {"start": v(-518.33, 16.54) * mm, "end": v(-518.33, 10.19) * mm});
            skLineSegment(sketch, "E338", {"start": v(-518.33, 10.19) * mm, "end": v(-542.46, 10.19) * mm});
            skLineSegment(sketch, "E339", {"start": v(-542.46, 10.19) * mm, "end": v(-542.46, 22.89) * mm});
            skLineSegment(sketch, "E340", {"start": v(-542.46, 22.89) * mm, "end": v(-511.98, 22.89) * mm});
            skLineSegment(sketch, "E341", {"start": v(-511.98, 22.89) * mm, "end": v(-511.98, 40.67) * mm});
            skLineSegment(sketch, "E342", {"start": v(-511.98, 40.67) * mm, "end": v(-518.33, 40.67) * mm});
            skLineSegment(sketch, "E343", {"start": v(-518.33, 40.67) * mm, "end": v(-518.33, 34.32) * mm});
            skLineSegment(sketch, "E344", {"start": v(-518.33, 34.32) * mm, "end": v(-542.46, 34.32) * mm});
            skLineSegment(sketch, "E345", {"start": v(-542.46, 34.32) * mm, "end": v(-542.46, 47.02) * mm});
            skLineSegment(sketch, "E346", {"start": v(-466.26, -80.05) * mm, "end": v(-466.26, -73.63) * mm});
            skLineSegment(sketch, "E347", {"start": v(-466.26, -73.63) * mm, "end": v(-496.74, -73.63) * mm});
            skLineSegment(sketch, "E348", {"start": v(-496.74, -73.63) * mm, "end": v(-496.74, -55.85) * mm});
            skLineSegment(sketch, "E349", {"start": v(-496.74, -55.85) * mm, "end": v(-490.39, -55.85) * mm});
            skLineSegment(sketch, "E350", {"start": v(-490.39, -55.85) * mm, "end": v(-490.39, -62.2) * mm});
            skLineSegment(sketch, "E351", {"start": v(-490.39, -62.2) * mm, "end": v(-466.26, -62.2) * mm});
            skLineSegment(sketch, "E352", {"start": v(-466.26, -62.2) * mm, "end": v(-466.26, -49.5) * mm});
            skLineSegment(sketch, "E353", {"start": v(-466.26, -49.5) * mm, "end": v(-496.74, -49.5) * mm});
            skLineSegment(sketch, "E354", {"start": v(-496.74, -49.5) * mm, "end": v(-496.74, -31.72) * mm});
            skLineSegment(sketch, "E355", {"start": v(-496.74, -31.72) * mm, "end": v(-490.39, -31.72) * mm});
            skLineSegment(sketch, "E356", {"start": v(-490.39, -31.72) * mm, "end": v(-490.39, -38.07) * mm});
            skLineSegment(sketch, "E357", {"start": v(-490.39, -38.07) * mm, "end": v(-466.26, -38.07) * mm});
            skLineSegment(sketch, "E358", {"start": v(-466.26, -38.07) * mm, "end": v(-466.26, -25.37) * mm});
            skLineSegment(sketch, "E359", {"start": v(-466.26, -25.37) * mm, "end": v(-496.74, -25.37) * mm});
            skLineSegment(sketch, "E360", {"start": v(-496.74, -25.37) * mm, "end": v(-496.74, -7.6) * mm});
            skLineSegment(sketch, "E361", {"start": v(-496.74, -7.6) * mm, "end": v(-490.39, -7.6) * mm});
            skLineSegment(sketch, "E362", {"start": v(-490.39, -7.6) * mm, "end": v(-490.39, -13.94) * mm});
            skLineSegment(sketch, "E363", {"start": v(-490.39, -13.94) * mm, "end": v(-466.26, -13.94) * mm});
            skLineSegment(sketch, "E364", {"start": v(-466.26, -13.94) * mm, "end": v(-466.26, -1.24) * mm});
            skLineSegment(sketch, "E365", {"start": v(-466.26, -1.24) * mm, "end": v(-496.74, -1.24) * mm});
            skLineSegment(sketch, "E366", {"start": v(-496.74, -1.24) * mm, "end": v(-496.74, 16.54) * mm});
            skLineSegment(sketch, "E367", {"start": v(-496.74, 16.54) * mm, "end": v(-490.39, 16.54) * mm});
            skLineSegment(sketch, "E368", {"start": v(-490.39, 16.54) * mm, "end": v(-490.39, 10.19) * mm});
            skLineSegment(sketch, "E369", {"start": v(-490.39, 10.19) * mm, "end": v(-466.26, 10.19) * mm});
            skLineSegment(sketch, "E370", {"start": v(-466.26, 10.19) * mm, "end": v(-466.26, 22.89) * mm});
            skLineSegment(sketch, "E371", {"start": v(-466.26, 22.89) * mm, "end": v(-496.74, 22.89) * mm});
            skLineSegment(sketch, "E372", {"start": v(-496.74, 22.89) * mm, "end": v(-496.74, 40.67) * mm});
            skLineSegment(sketch, "E373", {"start": v(-496.74, 40.67) * mm, "end": v(-490.39, 40.67) * mm});
            skLineSegment(sketch, "E374", {"start": v(-490.39, 40.67) * mm, "end": v(-490.39, 34.32) * mm});
            skLineSegment(sketch, "E375", {"start": v(-490.39, 34.32) * mm, "end": v(-466.26, 34.32) * mm});
            skLineSegment(sketch, "E376", {"start": v(-466.26, 34.32) * mm, "end": v(-466.26, 47.02) * mm});
            skLineSegment(sketch, "E377", {"start": v(-511.98, -73.63) * mm, "end": v(-511.98, -55.85) * mm});
            skLineSegment(sketch, "E378", {"start": v(-518.33, -62.2) * mm, "end": v(-518.33, -55.85) * mm});
            skLineSegment(sketch, "E379", {"start": v(-518.33, -55.85) * mm, "end": v(-511.98, -55.85) * mm});
            skLineSegment(sketch, "E380", {"start": v(-511.98, -73.63) * mm, "end": v(-542.46, -73.63) * mm});
            skLineSegment(sketch, "E381", {"start": v(-542.46, -62.2) * mm, "end": v(-542.46, -49.5) * mm});
            skLineSegment(sketch, "E382", {"start": v(-542.46, -73.63) * mm, "end": v(-542.46, -80.05) * mm});
            skLineSegment(sketch, "E383", {"start": v(-542.46, -62.2) * mm, "end": v(-518.33, -62.2) * mm});
            skLineSegment(sketch, "E384", {"start": v(-542.46, -80.05) * mm, "end": v(-466.26, -80.05) * mm});
            skPoint(sketch, "E385", {"position": v(-504.36, -80.05) * mm});
            skLineSegment(sketch, "E386", {"start": v(-272.58, 71.15) * mm, "end": v(-259.88, 71.15) * mm});
            skPoint(sketch, "E387", {"position": v(-266.23, 71.15) * mm});
            skLineSegment(sketch, "E388", {"start": v(-542.46, 47.02) * mm, "end": v(-511.98, 47.02) * mm});
            skLineSegment(sketch, "E389", {"start": v(-511.98, 47.02) * mm, "end": v(-511.98, 64.8) * mm});
            skLineSegment(sketch, "E390", {"start": v(-511.98, 64.8) * mm, "end": v(-518.33, 64.8) * mm});
            skLineSegment(sketch, "E391", {"start": v(-518.33, 64.8) * mm, "end": v(-518.33, 58.45) * mm});
            skLineSegment(sketch, "E392", {"start": v(-518.33, 58.45) * mm, "end": v(-542.46, 58.45) * mm});
            skLineSegment(sketch, "E393", {"start": v(-542.46, 58.45) * mm, "end": v(-542.46, 71.15) * mm});
            skLineSegment(sketch, "E394", {"start": v(-542.46, 71.15) * mm, "end": v(-511.98, 71.15) * mm});
            skLineSegment(sketch, "E395", {"start": v(-511.98, 88.93) * mm, "end": v(-518.33, 88.93) * mm});
            skLineSegment(sketch, "E396", {"start": v(-518.33, 88.93) * mm, "end": v(-518.33, 82.58) * mm});
            skLineSegment(sketch, "E397", {"start": v(-518.33, 82.58) * mm, "end": v(-542.46, 82.58) * mm});
            skLineSegment(sketch, "E398", {"start": v(-542.46, 82.58) * mm, "end": v(-542.46, 95.28) * mm});
            skLineSegment(sketch, "E399", {"start": v(-466.26, 47.02) * mm, "end": v(-496.74, 47.02) * mm});
            skLineSegment(sketch, "E400", {"start": v(-496.74, 47.02) * mm, "end": v(-496.74, 64.8) * mm});
            skLineSegment(sketch, "E401", {"start": v(-496.74, 64.8) * mm, "end": v(-490.39, 64.8) * mm});
            skLineSegment(sketch, "E402", {"start": v(-490.39, 64.8) * mm, "end": v(-490.39, 58.45) * mm});
            skLineSegment(sketch, "E403", {"start": v(-490.39, 58.45) * mm, "end": v(-466.26, 58.45) * mm});
            skLineSegment(sketch, "E404", {"start": v(-466.26, 58.45) * mm, "end": v(-466.26, 71.15) * mm});
            skLineSegment(sketch, "E405", {"start": v(-466.26, 71.15) * mm, "end": v(-496.74, 71.15) * mm});
            skLineSegment(sketch, "E406", {"start": v(-496.74, 71.15) * mm, "end": v(-496.74, 88.93) * mm});
            skLineSegment(sketch, "E407", {"start": v(-496.74, 88.93) * mm, "end": v(-490.39, 88.93) * mm});
            skLineSegment(sketch, "E408", {"start": v(-490.39, 88.93) * mm, "end": v(-490.39, 82.58) * mm});
            skLineSegment(sketch, "E409", {"start": v(-490.39, 82.58) * mm, "end": v(-466.26, 82.58) * mm});
            skLineSegment(sketch, "E410", {"start": v(-466.26, 82.58) * mm, "end": v(-466.26, 95.28) * mm});
            skLineSegment(sketch, "E411", {"start": v(-511.98, 71.15) * mm, "end": v(-511.98, 88.93) * mm});
            skLineSegment(sketch, "E412", {"start": v(-542.46, 95.28) * mm, "end": v(-466.26, 95.28) * mm});
            skPoint(sketch, "E413", {"position": v(-504.36, 95.28) * mm});
            skLineSegment(sketch, "E414", {"start": v(-453.56, 47.02) * mm, "end": v(-423.08, 47.02) * mm});
            skLineSegment(sketch, "E415", {"start": v(-423.08, 47.02) * mm, "end": v(-423.08, 64.8) * mm});
            skLineSegment(sketch, "E416", {"start": v(-423.08, 64.8) * mm, "end": v(-429.43, 64.8) * mm});
            skLineSegment(sketch, "E417", {"start": v(-429.43, 64.8) * mm, "end": v(-429.43, 58.45) * mm});
            skLineSegment(sketch, "E418", {"start": v(-429.43, 58.45) * mm, "end": v(-453.56, 58.45) * mm});
            skLineSegment(sketch, "E419", {"start": v(-453.56, 58.45) * mm, "end": v(-453.56, 71.15) * mm});
            skLineSegment(sketch, "E420", {"start": v(-453.56, 71.15) * mm, "end": v(-423.08, 71.15) * mm});
            skLineSegment(sketch, "E421", {"start": v(-423.08, 88.93) * mm, "end": v(-429.43, 88.93) * mm});
            skLineSegment(sketch, "E422", {"start": v(-429.43, 88.93) * mm, "end": v(-429.43, 82.58) * mm});
            skLineSegment(sketch, "E423", {"start": v(-429.43, 82.58) * mm, "end": v(-453.56, 82.58) * mm});
            skLineSegment(sketch, "E424", {"start": v(-453.56, 82.58) * mm, "end": v(-453.56, 95.28) * mm});
            skLineSegment(sketch, "E425", {"start": v(-377.36, 47.02) * mm, "end": v(-407.84, 47.02) * mm});
            skLineSegment(sketch, "E426", {"start": v(-407.84, 47.02) * mm, "end": v(-407.84, 64.8) * mm});
            skLineSegment(sketch, "E427", {"start": v(-407.84, 64.8) * mm, "end": v(-401.49, 64.8) * mm});
            skLineSegment(sketch, "E428", {"start": v(-401.49, 64.8) * mm, "end": v(-401.49, 58.45) * mm});
            skLineSegment(sketch, "E429", {"start": v(-401.49, 58.45) * mm, "end": v(-377.36, 58.45) * mm});
            skLineSegment(sketch, "E430", {"start": v(-377.36, 58.45) * mm, "end": v(-377.36, 71.15) * mm});
            skLineSegment(sketch, "E431", {"start": v(-377.36, 71.15) * mm, "end": v(-407.84, 71.15) * mm});
            skLineSegment(sketch, "E432", {"start": v(-407.84, 71.15) * mm, "end": v(-407.84, 88.93) * mm});
            skLineSegment(sketch, "E433", {"start": v(-407.84, 88.93) * mm, "end": v(-401.49, 88.93) * mm});
            skLineSegment(sketch, "E434", {"start": v(-401.49, 88.93) * mm, "end": v(-401.49, 82.58) * mm});
            skLineSegment(sketch, "E435", {"start": v(-401.49, 82.58) * mm, "end": v(-377.36, 82.58) * mm});
            skLineSegment(sketch, "E436", {"start": v(-377.36, 82.58) * mm, "end": v(-377.36, 95.28) * mm});
            skLineSegment(sketch, "E437", {"start": v(-423.08, 71.15) * mm, "end": v(-423.08, 88.93) * mm});
            skLineSegment(sketch, "E438", {"start": v(-453.56, 95.28) * mm, "end": v(-377.36, 95.28) * mm});
            skPoint(sketch, "E439", {"position": v(-415.46, 95.28) * mm});
            skLineSegment(sketch, "E440", {"start": v(-364.66, 47.02) * mm, "end": v(-334.18, 47.02) * mm});
            skLineSegment(sketch, "E441", {"start": v(-334.18, 47.02) * mm, "end": v(-334.18, 64.8) * mm});
            skLineSegment(sketch, "E442", {"start": v(-334.18, 64.8) * mm, "end": v(-340.53, 64.8) * mm});
            skLineSegment(sketch, "E443", {"start": v(-340.53, 64.8) * mm, "end": v(-340.53, 58.45) * mm});
            skLineSegment(sketch, "E444", {"start": v(-340.53, 58.45) * mm, "end": v(-364.66, 58.45) * mm});
            skLineSegment(sketch, "E445", {"start": v(-364.66, 58.45) * mm, "end": v(-364.66, 71.15) * mm});
            skLineSegment(sketch, "E446", {"start": v(-364.66, 71.15) * mm, "end": v(-334.18, 71.15) * mm});
            skLineSegment(sketch, "E447", {"start": v(-334.18, 88.93) * mm, "end": v(-340.53, 88.93) * mm});
            skLineSegment(sketch, "E448", {"start": v(-340.53, 88.93) * mm, "end": v(-340.53, 82.58) * mm});
            skLineSegment(sketch, "E449", {"start": v(-340.53, 82.58) * mm, "end": v(-364.66, 82.58) * mm});
            skLineSegment(sketch, "E450", {"start": v(-364.66, 82.58) * mm, "end": v(-364.66, 95.28) * mm});
            skLineSegment(sketch, "E451", {"start": v(-288.46, 47.02) * mm, "end": v(-318.94, 47.02) * mm});
            skLineSegment(sketch, "E452", {"start": v(-318.94, 47.02) * mm, "end": v(-318.94, 64.8) * mm});
            skLineSegment(sketch, "E453", {"start": v(-318.94, 64.8) * mm, "end": v(-312.59, 64.8) * mm});
            skLineSegment(sketch, "E454", {"start": v(-312.59, 64.8) * mm, "end": v(-312.59, 58.45) * mm});
            skLineSegment(sketch, "E455", {"start": v(-312.59, 58.45) * mm, "end": v(-288.46, 58.45) * mm});
            skLineSegment(sketch, "E456", {"start": v(-288.46, 58.45) * mm, "end": v(-288.46, 71.15) * mm});
            skLineSegment(sketch, "E457", {"start": v(-288.46, 71.15) * mm, "end": v(-318.94, 71.15) * mm});
            skLineSegment(sketch, "E458", {"start": v(-318.94, 71.15) * mm, "end": v(-318.94, 88.93) * mm});
            skLineSegment(sketch, "E459", {"start": v(-318.94, 88.93) * mm, "end": v(-312.59, 88.93) * mm});
            skLineSegment(sketch, "E460", {"start": v(-312.59, 88.93) * mm, "end": v(-312.59, 82.58) * mm});
            skLineSegment(sketch, "E461", {"start": v(-312.59, 82.58) * mm, "end": v(-288.46, 82.58) * mm});
            skLineSegment(sketch, "E462", {"start": v(-288.46, 82.58) * mm, "end": v(-288.46, 95.28) * mm});
            skLineSegment(sketch, "E463", {"start": v(-334.18, 71.15) * mm, "end": v(-334.18, 88.93) * mm});
            skLineSegment(sketch, "E464", {"start": v(-364.66, 95.28) * mm, "end": v(-288.46, 95.28) * mm});
            skPoint(sketch, "E465", {"position": v(-326.56, 95.28) * mm});
            skLineSegment(sketch, "E466", {"start": v(-275.76, 47.02) * mm, "end": v(-245.28, 47.02) * mm});
            skLineSegment(sketch, "E467", {"start": v(-245.28, 47.02) * mm, "end": v(-245.28, 64.8) * mm});
            skLineSegment(sketch, "E468", {"start": v(-245.28, 64.8) * mm, "end": v(-251.63, 64.8) * mm});
            skLineSegment(sketch, "E469", {"start": v(-251.63, 64.8) * mm, "end": v(-251.63, 58.45) * mm});
            skLineSegment(sketch, "E470", {"start": v(-251.63, 58.45) * mm, "end": v(-275.76, 58.45) * mm});
            skLineSegment(sketch, "E471", {"start": v(-275.76, 58.45) * mm, "end": v(-275.76, 71.15) * mm});
            skLineSegment(sketch, "E472", {"start": v(-275.76, 71.15) * mm, "end": v(-245.28, 71.15) * mm});
            skLineSegment(sketch, "E473", {"start": v(-245.28, 88.93) * mm, "end": v(-251.63, 88.93) * mm});
            skLineSegment(sketch, "E474", {"start": v(-251.63, 88.93) * mm, "end": v(-251.63, 82.58) * mm});
            skLineSegment(sketch, "E475", {"start": v(-251.63, 82.58) * mm, "end": v(-275.76, 82.58) * mm});
            skLineSegment(sketch, "E476", {"start": v(-275.76, 82.58) * mm, "end": v(-275.76, 95.28) * mm});
            skLineSegment(sketch, "E477", {"start": v(-199.56, 47.02) * mm, "end": v(-230.04, 47.02) * mm});
            skLineSegment(sketch, "E478", {"start": v(-230.04, 47.02) * mm, "end": v(-230.04, 64.8) * mm});
            skLineSegment(sketch, "E479", {"start": v(-230.04, 64.8) * mm, "end": v(-223.69, 64.8) * mm});
            skLineSegment(sketch, "E480", {"start": v(-223.69, 64.8) * mm, "end": v(-223.69, 58.45) * mm});
            skLineSegment(sketch, "E481", {"start": v(-223.69, 58.45) * mm, "end": v(-199.56, 58.45) * mm});
            skLineSegment(sketch, "E482", {"start": v(-199.56, 58.45) * mm, "end": v(-199.56, 71.15) * mm});
            skLineSegment(sketch, "E483", {"start": v(-199.56, 71.15) * mm, "end": v(-230.04, 71.15) * mm});
            skLineSegment(sketch, "E484", {"start": v(-230.04, 71.15) * mm, "end": v(-230.04, 88.93) * mm});
            skLineSegment(sketch, "E485", {"start": v(-230.04, 88.93) * mm, "end": v(-223.69, 88.93) * mm});
            skLineSegment(sketch, "E486", {"start": v(-223.69, 88.93) * mm, "end": v(-223.69, 82.58) * mm});
            skLineSegment(sketch, "E487", {"start": v(-223.69, 82.58) * mm, "end": v(-199.56, 82.58) * mm});
            skLineSegment(sketch, "E488", {"start": v(-199.56, 82.58) * mm, "end": v(-199.56, 95.28) * mm});
            skLineSegment(sketch, "E489", {"start": v(-245.28, 71.15) * mm, "end": v(-245.28, 88.93) * mm});
            skLineSegment(sketch, "E490", {"start": v(-275.76, 95.28) * mm, "end": v(-199.56, 95.28) * mm});
            skPoint(sketch, "E491", {"position": v(-237.66, 95.28) * mm});
            skLineSegment(sketch, "E492", {"start": v(-186.86, 47.02) * mm, "end": v(-156.38, 47.02) * mm});
            skLineSegment(sketch, "E493", {"start": v(-156.38, 47.02) * mm, "end": v(-156.38, 64.8) * mm});
            skLineSegment(sketch, "E494", {"start": v(-156.38, 64.8) * mm, "end": v(-162.73, 64.8) * mm});
            skLineSegment(sketch, "E495", {"start": v(-162.73, 64.8) * mm, "end": v(-162.73, 58.45) * mm});
            skLineSegment(sketch, "E496", {"start": v(-162.73, 58.45) * mm, "end": v(-186.86, 58.45) * mm});
            skLineSegment(sketch, "E497", {"start": v(-186.86, 58.45) * mm, "end": v(-186.86, 71.15) * mm});
            skLineSegment(sketch, "E498", {"start": v(-186.86, 71.15) * mm, "end": v(-156.38, 71.15) * mm});
            skLineSegment(sketch, "E499", {"start": v(-156.38, 88.93) * mm, "end": v(-162.73, 88.93) * mm});
            skLineSegment(sketch, "E500", {"start": v(-162.73, 88.93) * mm, "end": v(-162.73, 82.58) * mm});
            skLineSegment(sketch, "E501", {"start": v(-162.73, 82.58) * mm, "end": v(-186.86, 82.58) * mm});
            skLineSegment(sketch, "E502", {"start": v(-186.86, 82.58) * mm, "end": v(-186.86, 95.28) * mm});
            skLineSegment(sketch, "E503", {"start": v(-110.66, 47.02) * mm, "end": v(-141.14, 47.02) * mm});
            skLineSegment(sketch, "E504", {"start": v(-141.14, 47.02) * mm, "end": v(-141.14, 64.8) * mm});
            skLineSegment(sketch, "E505", {"start": v(-141.14, 64.8) * mm, "end": v(-134.79, 64.8) * mm});
            skLineSegment(sketch, "E506", {"start": v(-134.79, 64.8) * mm, "end": v(-134.79, 58.45) * mm});
            skLineSegment(sketch, "E507", {"start": v(-134.79, 58.45) * mm, "end": v(-110.66, 58.45) * mm});
            skLineSegment(sketch, "E508", {"start": v(-110.66, 58.45) * mm, "end": v(-110.66, 71.15) * mm});
            skLineSegment(sketch, "E509", {"start": v(-110.66, 71.15) * mm, "end": v(-141.14, 71.15) * mm});
            skLineSegment(sketch, "E510", {"start": v(-141.14, 71.15) * mm, "end": v(-141.14, 88.93) * mm});
            skLineSegment(sketch, "E511", {"start": v(-141.14, 88.93) * mm, "end": v(-134.79, 88.93) * mm});
            skLineSegment(sketch, "E512", {"start": v(-134.79, 88.93) * mm, "end": v(-134.79, 82.58) * mm});
            skLineSegment(sketch, "E513", {"start": v(-134.79, 82.58) * mm, "end": v(-110.66, 82.58) * mm});
            skLineSegment(sketch, "E514", {"start": v(-110.66, 82.58) * mm, "end": v(-110.66, 95.28) * mm});
            skLineSegment(sketch, "E515", {"start": v(-156.38, 71.15) * mm, "end": v(-156.38, 88.93) * mm});
            skLineSegment(sketch, "E516", {"start": v(-186.86, 95.28) * mm, "end": v(-110.66, 95.28) * mm});
            skPoint(sketch, "E517", {"position": v(-148.76, 95.28) * mm});
            skLineSegment(sketch, "E518", {"start": v(-97.96, 47.02) * mm, "end": v(-67.48, 47.02) * mm});
            skLineSegment(sketch, "E519", {"start": v(-67.48, 47.02) * mm, "end": v(-67.48, 64.8) * mm});
            skLineSegment(sketch, "E520", {"start": v(-67.48, 64.8) * mm, "end": v(-73.83, 64.8) * mm});
            skLineSegment(sketch, "E521", {"start": v(-73.83, 64.8) * mm, "end": v(-73.83, 58.45) * mm});
            skLineSegment(sketch, "E522", {"start": v(-73.83, 58.45) * mm, "end": v(-97.96, 58.45) * mm});
            skLineSegment(sketch, "E523", {"start": v(-97.96, 58.45) * mm, "end": v(-97.96, 71.15) * mm});
            skLineSegment(sketch, "E524", {"start": v(-97.96, 71.15) * mm, "end": v(-67.48, 71.15) * mm});
            skLineSegment(sketch, "E525", {"start": v(-67.48, 88.93) * mm, "end": v(-73.83, 88.93) * mm});
            skLineSegment(sketch, "E526", {"start": v(-73.83, 88.93) * mm, "end": v(-73.83, 82.58) * mm});
            skLineSegment(sketch, "E527", {"start": v(-73.83, 82.58) * mm, "end": v(-97.96, 82.58) * mm});
            skLineSegment(sketch, "E528", {"start": v(-97.96, 82.58) * mm, "end": v(-97.96, 95.28) * mm});
            skLineSegment(sketch, "E529", {"start": v(-21.76, 47.02) * mm, "end": v(-52.24, 47.02) * mm});
            skLineSegment(sketch, "E530", {"start": v(-52.24, 47.02) * mm, "end": v(-52.24, 64.8) * mm});
            skLineSegment(sketch, "E531", {"start": v(-52.24, 64.8) * mm, "end": v(-45.89, 64.8) * mm});
            skLineSegment(sketch, "E532", {"start": v(-45.89, 64.8) * mm, "end": v(-45.89, 58.45) * mm});
            skLineSegment(sketch, "E533", {"start": v(-45.89, 58.45) * mm, "end": v(-21.76, 58.45) * mm});
            skLineSegment(sketch, "E534", {"start": v(-21.76, 58.45) * mm, "end": v(-21.76, 71.15) * mm});
            skLineSegment(sketch, "E535", {"start": v(-21.76, 71.15) * mm, "end": v(-52.24, 71.15) * mm});
            skLineSegment(sketch, "E536", {"start": v(-52.24, 71.15) * mm, "end": v(-52.24, 88.93) * mm});
            skLineSegment(sketch, "E537", {"start": v(-52.24, 88.93) * mm, "end": v(-45.89, 88.93) * mm});
            skLineSegment(sketch, "E538", {"start": v(-45.89, 88.93) * mm, "end": v(-45.89, 82.58) * mm});
            skLineSegment(sketch, "E539", {"start": v(-45.89, 82.58) * mm, "end": v(-21.76, 82.58) * mm});
            skLineSegment(sketch, "E540", {"start": v(-21.76, 82.58) * mm, "end": v(-21.76, 95.28) * mm});
            skLineSegment(sketch, "E541", {"start": v(-67.48, 71.15) * mm, "end": v(-67.48, 88.93) * mm});
            skLineSegment(sketch, "E542", {"start": v(-97.96, 95.28) * mm, "end": v(-21.76, 95.28) * mm});
            skPoint(sketch, "E543", {"position": v(-59.86, 95.28) * mm});
            skSolve(sketch);
        }
        {
            var Q0;
            Q0=makeQuery(id+"F0.imprint","IMPRINT",FACE,{"disambiguationData":[TD([[makeQuery(id+"F0.imprint","IMPRINT",EDGE,{"derivedFrom":sQuery(id+"F0.wireOp",EDGE,"E0")}),1.0]])]});
            extrude(context, id + "F1", {"entities" : qUnion([Q0]), "depth" : 6.35 * mm});
        }
    });
